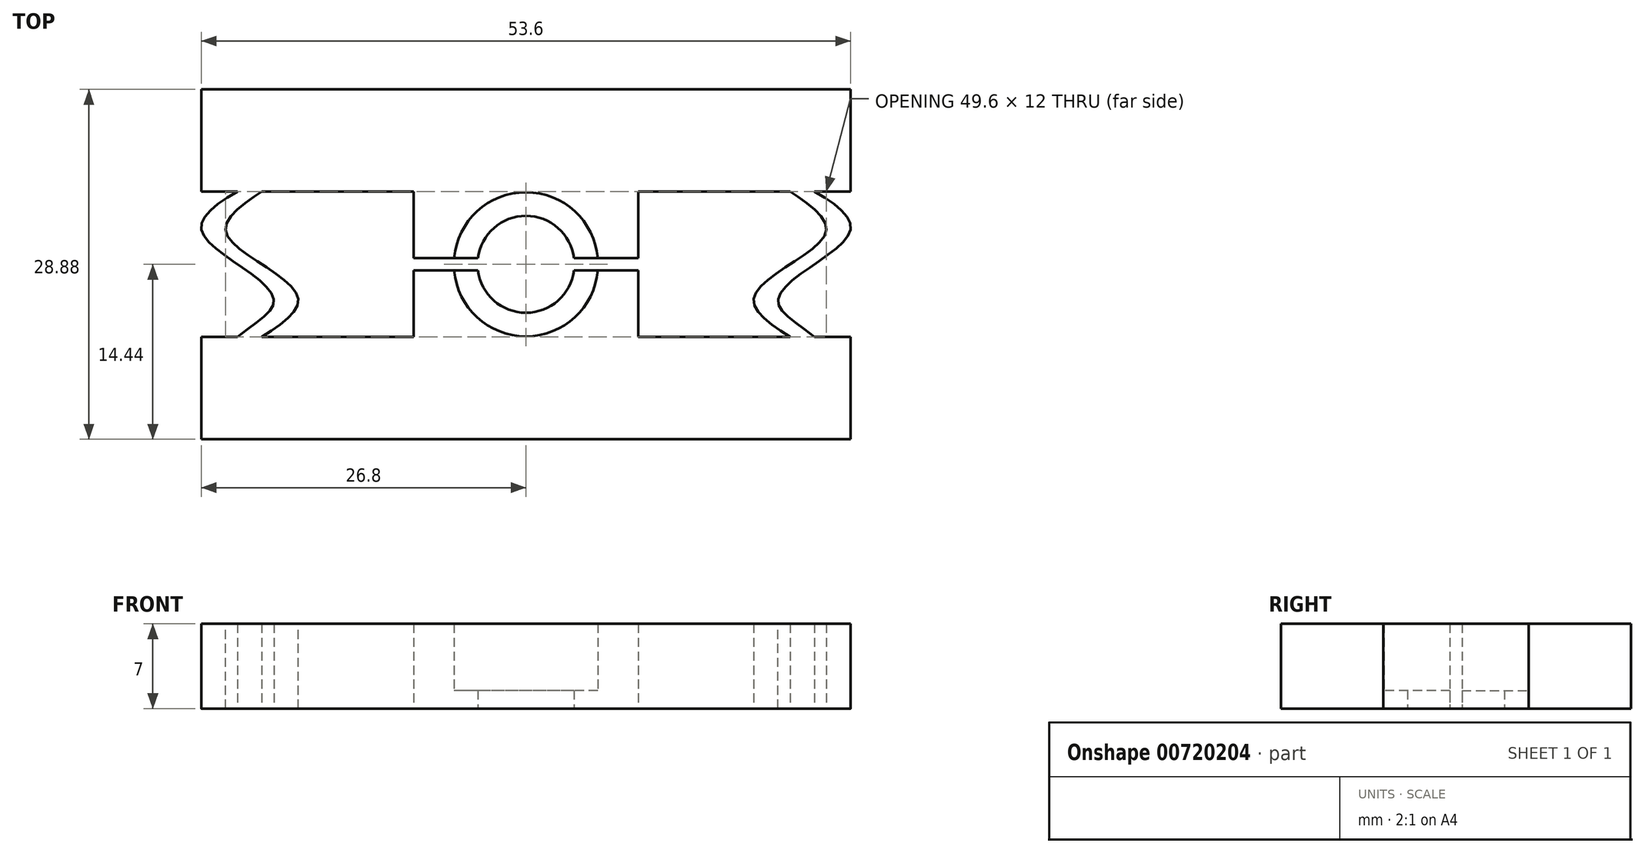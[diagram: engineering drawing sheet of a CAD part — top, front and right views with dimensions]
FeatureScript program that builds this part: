
annotation { "Feature Type Name" : "Feature", "Feature Type Description" : "" }
export const myFeature = defineFeature(function(context is Context, id is Id, definition is map)
    precondition{}
    {
        {
            var Q0;
            Q0=qCreatedBy(makeId("Front.planeOp"),FACE);
            var sketch = newSketch(context, id + "F0", { "sketchPlane" : qUnion([Q0])});
            skLineSegment(sketch, "E0", {"start": v(-31.97, -0.4) * mm, "end": v(-31.97, -7.4) * mm});
            skLineSegment(sketch, "E1", {"start": v(-31.97, -7.4) * mm, "end": v(-4, -7.4) * mm});
            skLineSegment(sketch, "E2", {"start": v(-31.97, -0.4) * mm, "end": v(-5.95, -0.4) * mm});
            skLineSegment(sketch, "E3", {"start": v(-5.95, -5.9) * mm, "end": v(-5.95, -0.4) * mm});
            skLineSegment(sketch, "E4", {"start": v(-5.95, -5.9) * mm, "end": v(-4, -5.9) * mm});
            skLineSegment(sketch, "E5", {"start": v(0, -17.84) * mm, "end": v(0, 5.1) * mm, "construction": true});
            skLineSegment(sketch, "E6", {"start": v(-4, -5.9) * mm, "end": v(-4, -7.4) * mm});
            skSolve(sketch);
        }
        {
            var Q0;
            Q0=makeQuery(id+"F0.imprint","IMPRINT",FACE,{"disambiguationData":[TD([[makeQuery(id+"F0.imprint","IMPRINT",EDGE,{"derivedFrom":sQuery(id+"F0.wireOp",EDGE,"E0")}),1.0]])]});
            var Q1;
            Q1=sQuery(id+"F0.wireOp",EDGE,"E5");
            revolve(context, id + "F1", {"surfaceOperationType" : NewSurfaceOperationType.NEW, "entities" : qUnion([Q0]), "axis" : qUnion([Q1]), "revolveType" : RevolveType.FULL});
        }
        {
            var Q0;
            Q0=makeQuery(id+"F1.opRevolve","SWEPT_FACE",FACE,{"disambiguationData":[OSD([sQuery(id+"F0.wireOp",EDGE,"E1")])]});
            var sketch = newSketch(context, id + "F2", { "sketchPlane" : qUnion([Q0])});
            skLineSegment(sketch, "E7.bottom", {"start": v(-26.8, 14.44) * mm, "end": v(26.8, 14.44) * mm});
            skLineSegment(sketch, "E7.top", {"start": v(-26.8, -14.44) * mm, "end": v(26.8, -14.44) * mm});
            skLineSegment(sketch, "E7.left", {"start": v(-26.8, 14.44) * mm, "end": v(-26.8, -14.44) * mm});
            skLineSegment(sketch, "E7.right", {"start": v(26.8, 14.44) * mm, "end": v(26.8, -14.44) * mm});
            skLineSegment(sketch, "E8.bottom", {"start": v(58.35, 36.08) * mm, "end": v(-55.21, 36.08) * mm});
            skLineSegment(sketch, "E8.top", {"start": v(58.35, -45.12) * mm, "end": v(-55.21, -45.12) * mm});
            skLineSegment(sketch, "E8.left", {"start": v(58.35, 36.08) * mm, "end": v(58.35, -45.12) * mm});
            skLineSegment(sketch, "E8.right", {"start": v(-55.21, 36.08) * mm, "end": v(-55.21, -45.12) * mm});
            skSolve(sketch);
        }
        {
            var Q0;
            Q0=makeQuery(id+"F2.imprint","IMPRINT",FACE,{"disambiguationData":[TD([[makeQuery(id+"F2.imprint","IMPRINT",EDGE,{"derivedFrom":sQuery(id+"F2.wireOp",EDGE,"E8.bottom")}),1.0]])]});
            var Q1;
            Q1=makeQuery(id+"F2.imprint","IMPRINT",FACE,{"disambiguationData":[TD([[makeQuery(id+"F2.imprint","IMPRINT",EDGE,{"derivedFrom":sQuery(id+"F2.wireOp",EDGE,"E7.bottom")}),1.0]])]});
            extrude(context, id + "F3", {"entities" : qUnion([Q0, Q1]), "operationType" : NewBodyOperationType.REMOVE, "oppositeDirection" : true, "depth" : 25 * mm, "offsetDistance" : 25 * mm});
        }
        {
            var Q0;
            Q0=makeQuery(id+"F1.opRevolve","SWEPT_FACE",FACE,{"disambiguationData":[OSD([sQuery(id+"F0.wireOp",EDGE,"E1")])]});
            var sketch = newSketch(context, id + "F4", { "sketchPlane" : qUnion([Q0])});
            skLineSegment(sketch, "E9.bottom", {"start": v(-9.28, 0.5) * mm, "end": v(9.28, 0.5) * mm});
            skLineSegment(sketch, "E9.top", {"start": v(-9.28, -0.5) * mm, "end": v(9.28, -0.5) * mm});
            skLineSegment(sketch, "E10.bottom", {"start": v(-28.52, 6) * mm, "end": v(-9.28, 6) * mm});
            skLineSegment(sketch, "E10.top", {"start": v(-28.52, -6) * mm, "end": v(-9.28, -6) * mm});
            skLineSegment(sketch, "E10.left", {"start": v(-28.52, 6) * mm, "end": v(-28.52, -6) * mm});
            skLineSegment(sketch, "E10.right", {"start": v(-9.28, 6) * mm, "end": v(-9.28, 0.5) * mm});
            skLineSegment(sketch, "E11.bottom", {"start": v(9.28, 6) * mm, "end": v(29.5, 6) * mm});
            skLineSegment(sketch, "E11.top", {"start": v(9.28, -6) * mm, "end": v(29.5, -6) * mm});
            skLineSegment(sketch, "E11.left", {"start": v(9.28, 6) * mm, "end": v(9.28, 0.5) * mm});
            skLineSegment(sketch, "E11.right", {"start": v(29.5, 6) * mm, "end": v(29.5, -6) * mm});
            skLineSegment(sketch, "E12.trimOffspring", {"start": v(-9.28, -0.5) * mm, "end": v(-9.28, -6) * mm});
            skLineSegment(sketch, "E13.trimOffspring", {"start": v(9.28, -0.5) * mm, "end": v(9.28, -6) * mm});
            skPoint(sketch, "E9.right.end.orphan", {"position": v(21.04, -0.5) * mm});
            skPoint(sketch, "E9.right.start.orphan", {"position": v(21.04, 0.5) * mm});
            skSolve(sketch);
        }
        {
            var Q0;
            {var subQ4=sQuery(id+"F4.wireOp",EDGE,"E10.right");Q0=makeQuery(id+"F4.imprint","IMPRINT",FACE,{"disambiguationData":[TD([[makeQuery(id+"F4.imprint","IMPRINT",EDGE,{"derivedFrom":subQ4}),-1.0]])]});}
            var Q1;
            {var subQ7=sQuery(id+"F4.wireOp",EDGE,"E11.left");Q1=makeQuery(id+"F4.imprint","IMPRINT",FACE,{"disambiguationData":[TD([[makeQuery(id+"F4.imprint","IMPRINT",EDGE,{"derivedFrom":subQ7}),1.0]])]});}
            var Q2;
            {var subQ0=sQuery(id+"F4.wireOp",EDGE,"E9.bottom");var subQ1=makeQuery(id+"F1.opRevolve","SWEPT_EDGE",EDGE,{"disambiguationData":[OSD([sQuery(id+"F0.wireOp",EDGE,"E1"),sQuery(id+"F0.wireOp",EDGE,"z0yT2Etd-mXlw-xgbI-E9AF-naOjWtuNQXBX")])]});var subQ2=makeQuery(id+"F4.imprint","INTERSECT",VERTEX,{"disambiguationData":[OD(0.0)],"derivedFrom":[subQ1,subQ0]});Q2=makeQuery(id+"F4.imprint","IMPRINT",FACE,{"disambiguationData":[TD([[makeQuery(id+"F4.imprint","IMPRINT",EDGE,{"disambiguationData":[TD([[subQ2,-1.0]])],"derivedFrom":subQ0}),-1.0]])]});}
            extrude(context, id + "F5", {"entities" : qUnion([Q0, Q1, Q2]), "operationType" : NewBodyOperationType.REMOVE, "oppositeDirection" : true, "depth" : 25 * mm, "offsetDistance" : 25 * mm});
        }
        {
            var Q0;
            Q0=makeQuery(id+"F5.boolean.opBoolean","SPLIT",FACE,{"disambiguationData":[TD([makeQuery(id+"F3.boolean.opBoolean","COPY",FACE,{"derivedFrom":makeQuery(id+"F3.opExtrude","SWEPT_FACE",FACE,{"disambiguationData":[OSD([sQuery(id+"F2.wireOp",EDGE,"E7.bottom")])]})})])],"derivedFrom":makeQuery(id+"F1.opRevolve","SWEPT_FACE",FACE,{"disambiguationData":[OSD([sQuery(id+"F0.wireOp",EDGE,"E1")])]})});
            var sketch = newSketch(context, id + "F6", { "sketchPlane" : qUnion([Q0])});
            skLineSegment(sketch, "E14", {"start": v(23.8, -17.08) * mm, "end": v(23.8, 16.86) * mm, "construction": true});
            skFitSpline(sketch, "E15", {"points": [v(23.8, 6) * mm, v(20.8, 3) * mm, v(23.8, 0) * mm, v(26.8, -3) * mm, v(23.8, -6) * mm], "startDerivative": vector(-19.08, -15.49) * mm, "endDerivative": vector(-20.67, -11.45) * mm});
            skLineSegment(sketch, "E16", {"start": v(21.8, 15.47) * mm, "end": v(21.8, -18.63) * mm, "construction": true});
            skLineSegment(sketch, "E17", {"start": v(21.8, 6) * mm, "end": v(23.8, 6) * mm});
            skFitSpline(sketch, "E18", {"points": [v(21.8, 6) * mm, v(18.8, 3) * mm, v(21.8, 0) * mm, v(24.8, -3) * mm, v(21.8, -6) * mm], "startDerivative": vector(-18.39, -11.54) * mm, "endDerivative": vector(-15.35, -9.69) * mm});
            skLineSegment(sketch, "E19", {"start": v(21.8, -6) * mm, "end": v(23.8, -6) * mm});
            skLineSegment(sketch, "E20.MirrorCS", {"start": v(-21.8, 6) * mm, "end": v(-23.8, 6) * mm});
            skLineSegment(sketch, "E21.MirrorCS", {"start": v(-21.8, -6) * mm, "end": v(-23.8, -6) * mm});
            skLineSegment(sketch, "E22.MirrorCS", {"start": v(-23.8, -17.08) * mm, "end": v(-23.8, 16.86) * mm, "construction": true});
            skLineSegment(sketch, "E23.MirrorCS", {"start": v(-21.8, 15.47) * mm, "end": v(-21.8, -18.63) * mm, "construction": true});
            skFitSpline(sketch, "E24.MirrorCS", {"points": [v(-21.8, 6) * mm, v(-18.8, 3) * mm, v(-21.8, 0) * mm, v(-24.8, -3) * mm, v(-21.8, -6) * mm], "startDerivative": vector(18.39, -11.54) * mm, "endDerivative": vector(15.35, -9.69) * mm});
            skFitSpline(sketch, "E25.MirrorCS", {"points": [v(-23.8, 6) * mm, v(-20.8, 3) * mm, v(-23.8, 0) * mm, v(-26.8, -3) * mm, v(-23.8, -6) * mm], "startDerivative": vector(19.08, -15.49) * mm, "endDerivative": vector(20.67, -11.45) * mm});
            skSolve(sketch);
        }
        {
            var Q0;
            Q0=makeQuery(id+"F6.imprint","IMPRINT",FACE,{"disambiguationData":[TD([[makeQuery(id+"F6.imprint","IMPRINT",EDGE,{"derivedFrom":sQuery(id+"F6.wireOp",EDGE,"E20.MirrorCS")}),-1.0]])]});
            var Q1;
            Q1=makeQuery(id+"F6.imprint","IMPRINT",FACE,{"disambiguationData":[TD([[makeQuery(id+"F6.imprint","IMPRINT",EDGE,{"derivedFrom":sQuery(id+"F6.wireOp",EDGE,"E15")}),-1.0]])]});
            var Q2;
            Q2=makeQuery(id+"F5.boolean.opBoolean","SPLIT",FACE,{"disambiguationData":[TD([makeQuery(id+"F3.boolean.opBoolean","COPY",FACE,{"derivedFrom":makeQuery(id+"F3.opExtrude","SWEPT_FACE",FACE,{"disambiguationData":[OSD([sQuery(id+"F2.wireOp",EDGE,"E7.top")])]})})])],"derivedFrom":makeQuery(id+"F1.opRevolve","SWEPT_FACE",FACE,{"disambiguationData":[OSD([sQuery(id+"F0.wireOp",EDGE,"E2")])]})});
            extrude(context, id + "F7", {"entities" : qUnion([Q0, Q1]), "operationType" : NewBodyOperationType.ADD, "endBound" : BoundingType.UP_TO_SURFACE, "oppositeDirection" : true, "depth" : 25 * mm, "endBoundEntityFace" : qUnion([Q2]), "offsetDistance" : 25 * mm});
        }
    });
